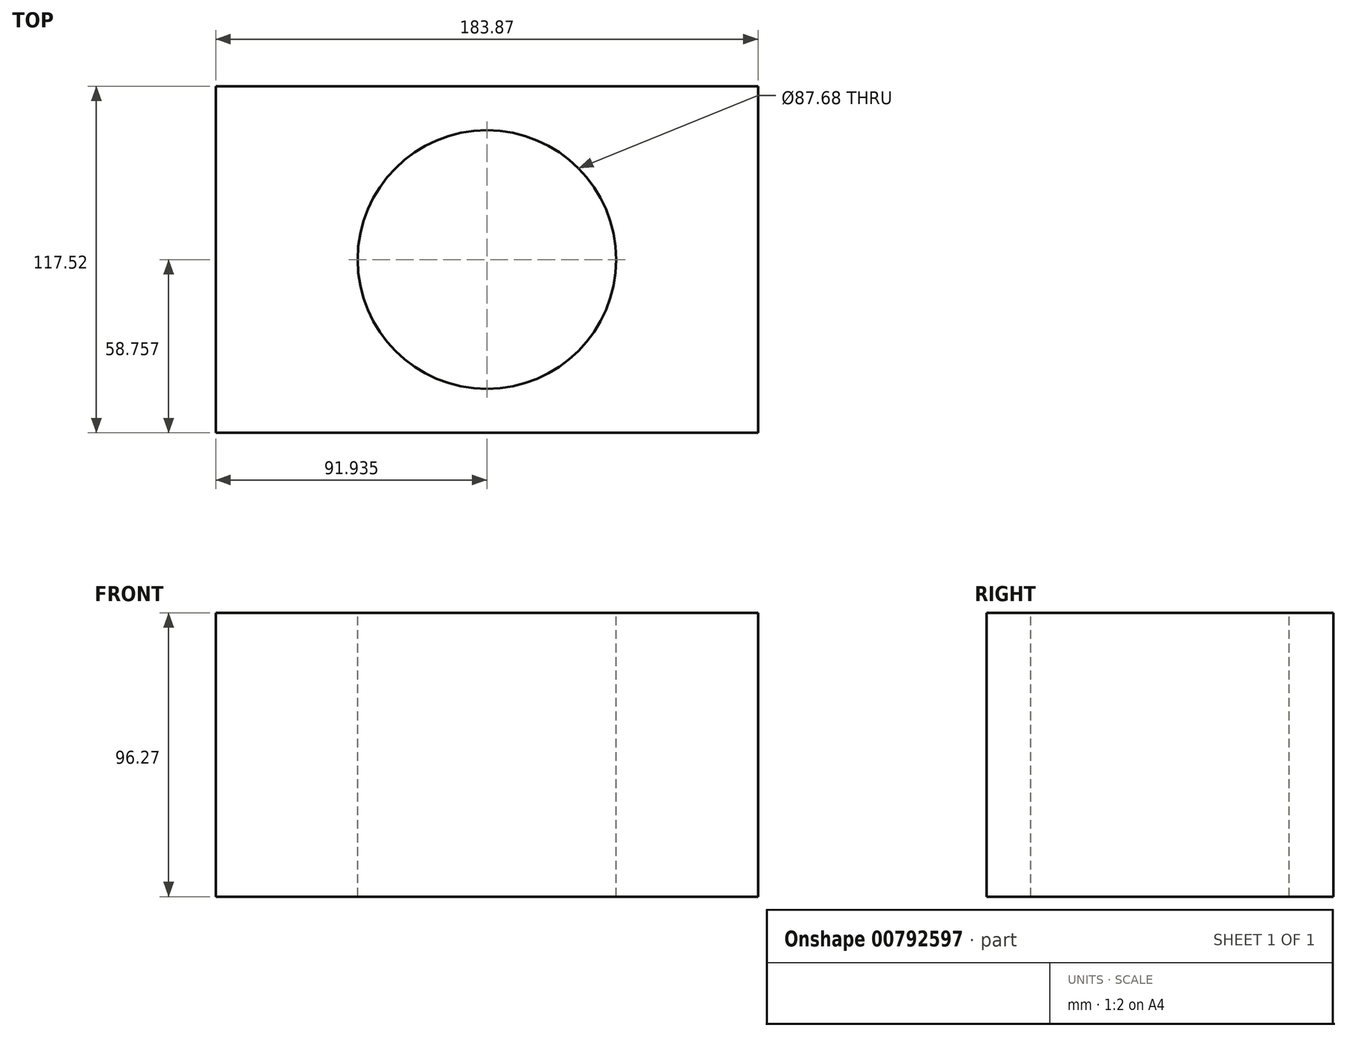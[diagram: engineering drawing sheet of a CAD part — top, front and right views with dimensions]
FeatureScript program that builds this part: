
annotation { "Feature Type Name" : "Feature", "Feature Type Description" : "" }
export const myFeature = defineFeature(function(context is Context, id is Id, definition is map)
    precondition{}
    {
        {
            var Q0;
            Q0=qCreatedBy(makeId("Top.planeOp"),FACE);
            var sketch = newSketch(context, id + "F0", { "sketchPlane" : qUnion([Q0])});
            skLineSegment(sketch, "E0.bottom", {"start": v(-90.84, 61.6) * mm, "end": v(93.03, 61.6) * mm});
            skLineSegment(sketch, "E0.top", {"start": v(-90.84, -55.91) * mm, "end": v(93.03, -55.91) * mm});
            skLineSegment(sketch, "E0.left", {"start": v(-90.84, 61.6) * mm, "end": v(-90.84, -55.91) * mm});
            skLineSegment(sketch, "E0.right", {"start": v(93.03, 61.6) * mm, "end": v(93.03, -55.91) * mm});
            skLineSegment(sketch, "E1", {"start": v(-90.84, 61.6) * mm, "end": v(93.03, -55.91) * mm, "construction": true});
            skLineSegment(sketch, "E2", {"start": v(93.03, 61.6) * mm, "end": v(-90.84, -55.91) * mm, "construction": true});
            skCircle(sketch, "E3", {"center": v(1.1, 2.85) * mm, "radius": 43.84 * mm});
            skLineSegment(sketch, "E4", {"start": v(1.1, 2.85) * mm, "end": v(1.1, 46.69) * mm, "construction": true});
            skLineSegment(sketch, "E5", {"start": v(1.1, -41) * mm, "end": v(1.1, 2.85) * mm, "construction": true});
            skLineSegment(sketch, "E6", {"start": v(44.93, 2.85) * mm, "end": v(-42.74, 2.85) * mm, "construction": true});
            skLineSegment(sketch, "E7", {"start": v(1.1, 46.69) * mm, "end": v(1.1, 107.88) * mm, "construction": true});
            skLineSegment(sketch, "E8", {"start": v(1.1, 107.88) * mm, "end": v(-90.84, 61.6) * mm});
            skLineSegment(sketch, "E9", {"start": v(1.1, 107.88) * mm, "end": v(93.03, 61.6) * mm});
            skSolve(sketch);
        }
        {
            var Q0;
            Q0=makeQuery(id+"F0.imprint","IMPRINT",FACE,{"disambiguationData":[TD([[makeQuery(id+"F0.imprint","IMPRINT",EDGE,{"derivedFrom":sQuery(id+"F0.wireOp",EDGE,"E0.bottom")}),-1.0]])]});
            extrude(context, id + "F1", {"entities" : qUnion([Q0]), "oppositeDirection" : true, "depth" : 96.27 * mm, "offsetDistance" : 25.4 * mm});
        }
    });
